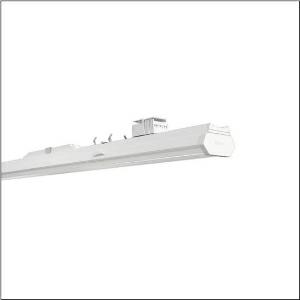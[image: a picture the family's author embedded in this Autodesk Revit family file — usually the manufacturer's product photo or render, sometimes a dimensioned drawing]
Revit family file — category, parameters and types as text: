
# Revit family: licross_r__11_protected_ho_51td1bmn4fxm_4fca
name_source: partatom
category: Lighting Fixtures
units: mm (PartAtom-declared; Revit-internal decimal feet)

## family parameters
Cut with Voids When Loaded = No
Host = Face
Light Source = No
Part Type = Normal
Room Calculation Point = No
Round Connector Dimension = Use Diameter
Shared = No

## types (1)
- --- (1 x LED, 15020 lm, 87.4 W, 4000K)
    Apparent Load = 87 VA
    CIE Flux Codes = 54 82 95 97 100
    Color Rendering = 80
    Color Temperature = 4000K
    Default Elevation = 1800 mm
    Description = Licross® 11 Protected HO, luminaire insert, of sheet steel, galvanised, coil coated, white, length: 1.500mm, width: 90mm, height: 101mm, LED rated luminous flux: 15.020lm, light colour: 840, control gear: ON/OFF Multilumen, with plug, 3-pole, with phase selection, mains connection: 220..240V, AC, 50/60Hz, rated input power: 87W, internal wiring halogen-free, primary optical cover: cover, of PMMA, light emission: direct distribution, primary light characteristic: symmetric, protection rating (complete): IP54, insulation class (complete): insulation class I (protective earthing), certification: CE, ENEC, VDE, UKCA, protection symbol: D if used in an environment with non-conductive dust loads with corresponding accessories, impact resistance: IK06, permissible ambient temperature for indoor applications: -35..+35°C, corresponds to IFS (International Featured Standards) requirements for safety and quality in the food industry, reducing of maximum allowable ambient temperature of 5°C with ceiling mounting, LABS conformity tested according to VDMA 24364:2018-05, packaging unit: 1 piece
    Height = 92 mm
    Lamp = 1 x LED
    Lamp Light Flux = 15020 lm
    Lamp Power = 87.4 W
    Lamp count = 1
    Length = 1500 mm
    Luminous efficacy = 172 lm/W
    Manufacturer = Siteco
    ModVariant = No
    Model = 51TD1BMN4FXM
    Mounting Place = Ceiling
    Mounting Type = Pendant
    Number of Poles = 1
    OnlyDefault = Yes
    Power Factor = 1
    Product Name = Licross® 11 Protected HO
    Product group = luminaire insert | ceiling pendant
    ProductGroupID = 902
    Protection Class = Protection class I
    Protection Degree = IP 54
    RLX_Detail_Level = 1
    RLX_Emergency_Light_Flux = 0 lm
    RLX_Emergency_Type = 0
    RLX_Emergency_Type_DB = No
    RlxData = <blob elided: 22065 chars, md5=5529acb5>
    Socket = socket
    Standby Power = 0 W
    System Light Flux = 15020 lm
    System Power = 87 W
    Type Comments = factory setting: luminous flux: 100 % | (A | C | E) | 203 mA
    Type Image = l_1256145.jpg
    URL = http://relux.com
    VarID = @adj_107571
    Voltage = 0 V
    Weight = 0.00 kg
    Width = 88 mm

## geometry (parser evidence)
native form markers: Blend x4, Sweep x9
no freeform markers — native parametric forms only
